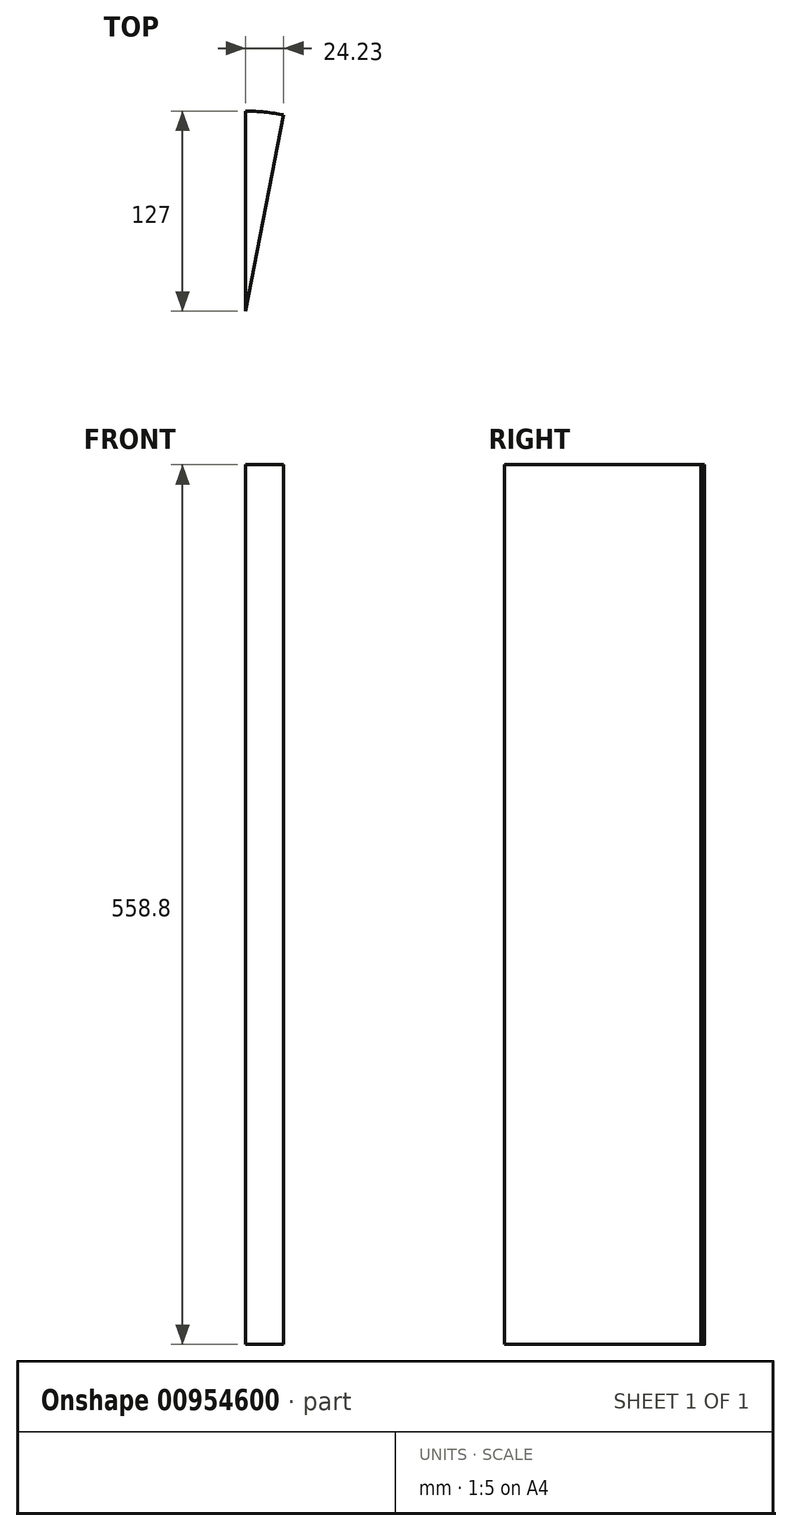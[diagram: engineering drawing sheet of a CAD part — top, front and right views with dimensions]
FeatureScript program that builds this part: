
annotation { "Feature Type Name" : "Feature", "Feature Type Description" : "" }
export const myFeature = defineFeature(function(context is Context, id is Id, definition is map)
    precondition{}
    {
        {
            var Q0;
            Q0=qCreatedBy(makeId("Top.planeOp"),FACE);
            var sketch = newSketch(context, id + "F0", { "sketchPlane" : qUnion([Q0])});
            skCircle(sketch, "E0", {"center": v(0, 0) * mm, "radius": 127 * mm});
            skSolve(sketch);
        }
        {
            var Q0;
            Q0=qCreatedBy(makeId("Top.planeOp"),FACE);
            var sketch = newSketch(context, id + "F1", { "sketchPlane" : qUnion([Q0])});
            skLineSegment(sketch, "E1", {"start": v(0, 0) * mm, "end": v(0, 127) * mm});
            skLineSegment(sketch, "E2", {"start": v(24.23, 124.67) * mm, "end": v(0, 0) * mm});
            skArc(sketch, "E3.0", {"start": v(24.23, 124.67) * mm, "mid": v(12.17, 126.42) * mm, "end": v(0, 127) * mm});
            skSolve(sketch);
        }
        {
            var Q0;
            Q0 = qSketchRegion(id + "F1", true);
            extrude(context, id + "F2", {"entities" : qUnion([Q0]), "depth" : 558.8 * mm, "offsetDistance" : 25.4 * mm});
        }
    });
